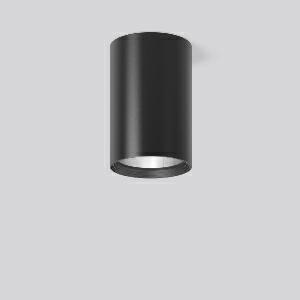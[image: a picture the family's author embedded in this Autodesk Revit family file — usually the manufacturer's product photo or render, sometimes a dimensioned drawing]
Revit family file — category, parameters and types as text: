
# Revit family: heledon_maxi_a_931247_003_2_76_8c8f
name_source: partatom
category: Lighting Fixtures
units: mm (PartAtom-declared; Revit-internal decimal feet)

## family parameters
Cut with Voids When Loaded = No
Host = Face
Light Source = No
Part Type = Normal
Room Calculation Point = No
Round Connector Dimension = Use Diameter
Shared = No

## types (1)
- HELEDON maxi A (1 x LED Modul 927 bakery, 3300 lm, 2700)
    Apparent Load = 33 VA
    Approval mark = CE
    CIE Flux Codes = 96 100 100 100 100
    Color Rendering = 90
    Color Temperature = 2700
    Default Elevation = 1800 mm
    Description = Series: HELEDON maxi
Cylindrical surface-mounted downlight. Housing: die-cast aluminium, powder-coated. Internal ceiling frame polycarbonate with bayonet mounting. Black plastic ring and recessed LED to prevent glare from the side. Optical assembly with reflector made of MIRO-Silver with 98% total light reflection for outstanding efficiency - can be changed without tools. Special LED for illumination of pastries included. Suitable for Ceiling mounting. Easy installation with a separate ceiling frame with bayonet mounting and plug connection. Driver integrated. Connected via plug-in connector. High quality converter without flickering and stroboscopic effect. The following accessories can be mounted without use of tools: interchangeable lenses, decorative glasses, honeycomb louvre, clear and frosted diffusers, white interchangeable plastic ring. 
Colour: deep black, matt (RAL 9005)
Diameter: 123 mm
Height: 183 mm
Lamp: LED
Socket: without socket
Colour temperature: bakery
Colour rendering index (CRI): 97
System power: 33 W
Rated luminous flux: 3300 lm
Luminous efficiency: 100 lm/W
Control gear: Converter, dimmable, DALI
Protection class: I
Type of protection: IP 20
    Height = 183 mm
    Lamp = 1 x LED Modul 927 bakery
    Lamp Light Flux = 3300 lm
    Lamp count = 1
    Length = 123 mm
    Lifetime = 50000 h
    Luminous efficacy = 100 lm/W
    Manufacturer = RZB
    ModVariant = No
    Model = 931247.003.2.76
    Mounting Place = Ceiling
    Mounting Type = Surface mounted
    Number of Poles = 1
    OnlyDefault = Yes
    Power Factor = 1
    Product Name = HELEDON maxi A
    Product group = Surface mounted downlights
    ProductGroupID = 302
    Protection Class = Protection class I
    Protection Degree = IP 20
    RLX_Detail_Level = 1
    RLX_Emergency_Light_Flux = 0 lm
    RLX_Emergency_Type = 0
    RLX_Emergency_Type_DB = No
    RlxData = <blob elided: 98485 chars, md5=c337acc3>
    Socket = socket
    Standby Power = 0 W
    System Light Flux = 3300 lm
    System Power = 33 W
    Type Comments = Product without accessories
    Type Image = 931192.003.jpg
    URL = http://relux.com
    VarID = ---
    Voltage = 230 V
    Voltage Range = 220-240 V
    Weight = 0.00 kg
    Width = 0 mm  [stored 0 ft]

note: [stored X ft] marks values corroborated as IEEE doubles in the binary element streams (Revit-internal decimal feet)

## geometry (parser evidence)
native form markers: Blend x4, Sweep x9
no freeform markers — native parametric forms only
